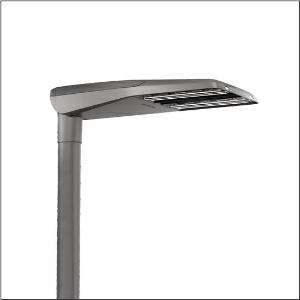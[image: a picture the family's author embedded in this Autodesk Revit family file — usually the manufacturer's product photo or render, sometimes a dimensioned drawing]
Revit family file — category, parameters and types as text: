
# Revit family: streetlight_sl_11_iq_midi___pc-r_5xc3f21f08me_be3f
name_source: partatom
category: Lighting Fixtures
units: mm (PartAtom-declared; Revit-internal decimal feet)

## family parameters
Cut with Voids When Loaded = No
Host = Face
Light Source = No
Part Type = Normal
Room Calculation Point = No
Round Connector Dimension = Use Diameter
Shared = No

## types (1)
- --- (1 x LED, 12740 lm, 124.7 W, 2200K)
    Apparent Load = 125 VA
    CIE Flux Codes = 37 73 96 100 100
    Color Rendering = 70
    Color Temperature = 2200K
    Default Elevation = 1800 mm
    Description = Streetlight SL 11 iQ midi, mast luminaire, primary light control with 3 zone facetted reflector, of plastic, silver coated, highly specular, primary optical cover: cover, of PMMA, transparent, light distribution: PC-R, light emission: direct distribution, primary light characteristic: asymmetric, right, installation type: post-top, side-entry, LED, High Power LED, rated luminous flux: 12.740lm, luminous efficacy: 102lm/W, light colour: 722, colour temperature: 2200K, control: Street-Remote, optimised constant luminous flux control (CLO 2.0), Desk-Remote (wireless, voltage-free reading and setting of iQ features in the workshop via application-optimized NFC function/RFID function), Light-Fading, Smart-Wire, Night-Set, Lumen-Switch, Temp-Guard, Auto-Match, with cable H07RN-F 5x 1.5mm², mains connection: 230..240V, AC, 50/60Hz, connection cable pre-assembled, cable length: 12,5m, start of lifetime: 125W, end of service life: 132W, reduction: 57W, luminaire housing, of diecast aluminium, powder-coated, Siteco® metallic grey (DB 702S), please order mast flange separately, inclination adjustable without tools: 0°, 5°, 10°, 15° (post-top) | 0°, -5°, -10°, -15° (side-entry), sealing non-destructively replaceable, multi-level sealing system, length: 780mm, width: 376mm, height: 118mm, mast flange for spigot size: 42mm (side-entry): 5XC10008XM4, 60/48mm (side-entry/post-top): 5XC10108XM2, 76/60mm (side-entry/post-top): 5XC10108XM1, equipment: Power, protection rating (complete): IP66, insulation class (complete): insulation class II (safety insulation), certification: CE, ENEC, VDE, impact resistance: IK09, permissible operating ambient temperature for outdoor applications: -25..+50°C, standard-compliant lighting for roads and squares, Environmental Product Declaration (EPD) tested and certified by an independent institute, packaging unit: 1 piece

Light Distribution: PC-R
    Height = 118 mm
    Lamp = 1 x LED
    Lamp Light Flux = 12740 lm
    Lamp Power = 124.7 W
    Lamp count = 1
    Length = 780 mm
    Luminous efficacy = 102 lm/W
    Manufacturer = Siteco
    ModVariant = No
    Model = 5XC3F21F08ME
    Number of Poles = 1
    OnlyDefault = Yes
    Power Factor = 1
    Product Name = Streetlight SL 11 iQ midi | PC-R
    Product group = mast luminaire | pylon top
    ProductGroupID = 6100
    Protection Class = Protection class II
    Protection Degree = IP 66
    RLX_Detail_Level = 1
    RLX_Emergency_Light_Flux = 0 lm
    RLX_Emergency_Type = 0
    RLX_Emergency_Type_DB = No
    RlxData = <blob elided: 74301 chars, md5=fff93ead>
    Socket = socket
    Standby Power = 0 W
    System Light Flux = 12741 lm
    System Power = 125 W
    Type Comments = factory setting: luminous flux: 100 % | dim-lin: 254 | 557 mA
    Type Image = l_1005960.jpg
    URL = http://relux.com
    VarID = @adj_058185
    Voltage = 0 V
    Weight = 0.00 kg
    Width = 376 mm

## geometry (parser evidence)
native form markers: Blend x4, Sweep x10
no freeform markers — native parametric forms only
